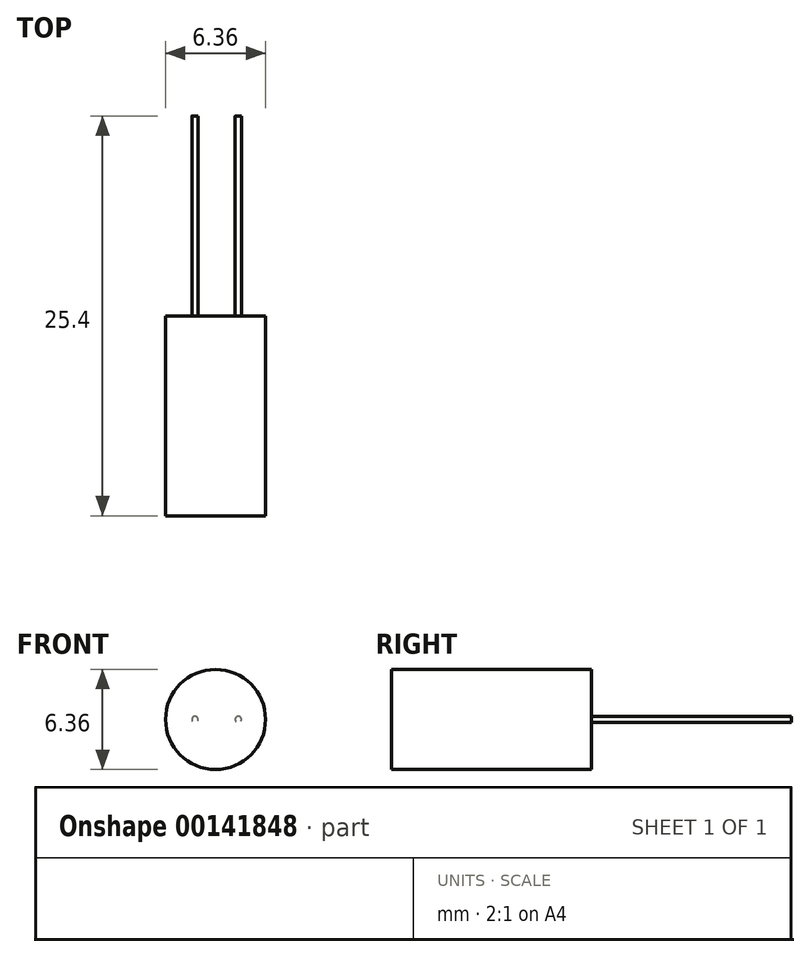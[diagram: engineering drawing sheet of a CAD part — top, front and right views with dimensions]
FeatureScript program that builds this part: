
annotation { "Feature Type Name" : "Feature", "Feature Type Description" : "" }
export const myFeature = defineFeature(function(context is Context, id is Id, definition is map)
    precondition{}
    {
        {
            var Q0;
            Q0=qCreatedBy(makeId("Front.planeOp"),FACE);
            var sketch = newSketch(context, id + "F0", { "sketchPlane" : qUnion([Q0])});
            skCircle(sketch, "E0", {"center": v(0, 0) * mm, "radius": 3.18 * mm});
            skSolve(sketch);
        }
        {
            var Q0;
            Q0 = qSketchRegion(id + "F0", true);
            extrude(context, id + "F1", {"entities" : qUnion([Q0]), "depth" : 12.7 * mm});
        }
        {
            var Q0;
            Q0=makeQuery(id+"F1.opExtrude","CAP_FACE",FACE,{"disambiguationData":[OSD([sQuery(id+"F0.wireOp",EDGE,"E0")])],"isStart":true});
            var sketch = newSketch(context, id + "F2", { "sketchPlane" : qUnion([Q0])});
            skCircle(sketch, "E1", {"center": v(1.3, 0) * mm, "radius": 0.2 * mm});
            skCircle(sketch, "E2", {"center": v(-1.45, 0) * mm, "radius": 0.2 * mm});
            skSolve(sketch);
        }
        {
            var Q0;
            Q0 = qSketchRegion(id + "F2", true);
            extrude(context, id + "F3", {"entities" : qUnion([Q0]), "depth" : 12.7 * mm});
        }
    });
